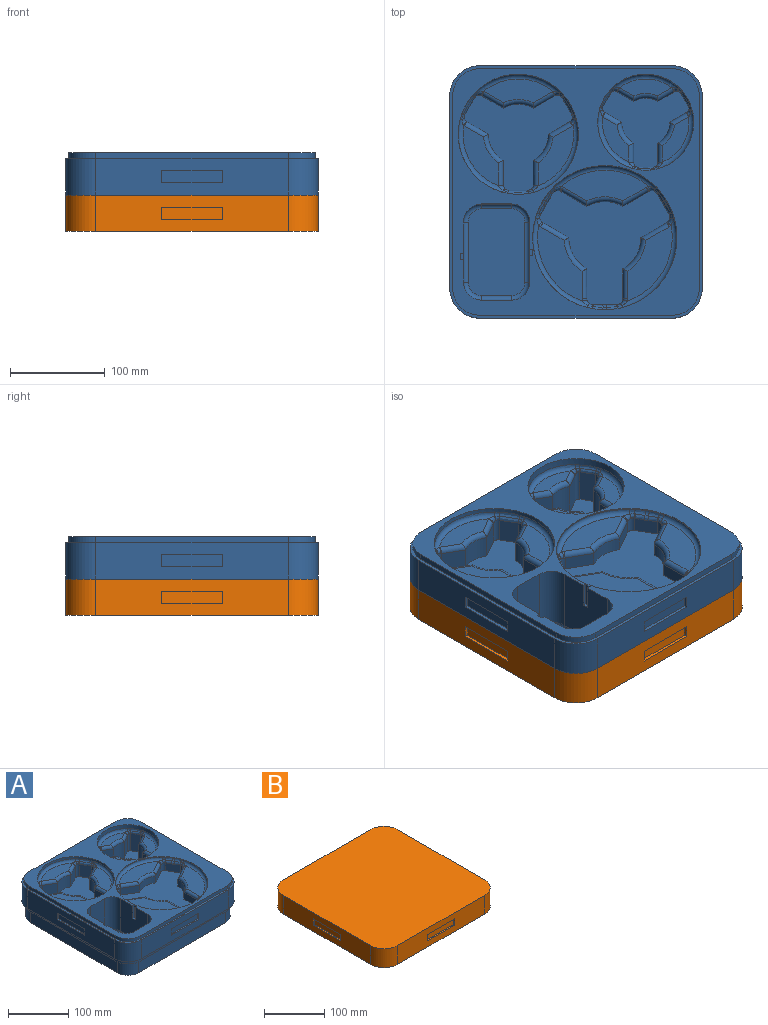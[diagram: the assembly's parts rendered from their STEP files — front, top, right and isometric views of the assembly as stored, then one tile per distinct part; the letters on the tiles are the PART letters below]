
ASSEMBLY  parts=2 mates=1
PART A: 313 faces, bbox 266.7x266.7x78.5 mm
  f0: plane 260.35x260.35mm, normal (0,0,1), area 21239.2mm2, adj f1,f17,f38,f59,f79,f80,f81,f82
  f1: plane 66.04x63.5mm, normal (-1,0,0), area 4032.2mm2, adj f0,f80,f81,f87,f309,f310,f312
  f2: plane 203.2x38.1mm, normal (1,0,0), area 6935.5mm2, adj f6,f9,f265,f274,f300,f301,f302,f303
  f3: plane 203.2x38.1mm, normal (0,1,0), area 6935.5mm2, adj f8,f9,f265,f274,f295,f296,f297,f298
  f4: plane 203.2x38.1mm, normal (-1,0,0), area 6935.5mm2, adj f7,f8,f265,f274,f290,f291,f292,f293
  f5: plane 203.2x38.1mm, normal (0,-1,0), area 6935.5mm2, adj f6,f7,f265,f274,f285,f286,f287,f288
  f6: cylinder r=31.75mm len=38.1mm, axis (0,0,1), area 1900.2mm2, adj f2,f5,f265,f274
  f7: cylinder r=31.75mm len=38.1mm, axis (0,0,1), area 1900.2mm2, adj f4,f5,f265,f274
  f8: cylinder r=31.75mm len=38.1mm, axis (0,0,1), area 1900.2mm2, adj f3,f4,f265,f274
  f9: cylinder r=31.75mm len=38.1mm, axis (0,0,1), area 1900.2mm2, adj f2,f3,f265,f274
  f10: plane 55.18x17.94mm, normal (0,0,1), area 651.1mm2, adj f131,f224,f226,f228
  f11: plane 47.78x27.94mm, normal (0,0,1), area 651.1mm2, adj f126,f229,f231,f233
  f12: plane 73.54x25.13mm, normal (0,0,1), area 1214.4mm2, adj f119,f184,f186,f188,f190,f192
  f13: plane 63.69x37.49mm, normal (0,0,1), area 1214.4mm2, adj f114,f189,f191,f193,f195,f197
  f14: plane 92.17x32.32mm, normal (0,0,1), area 1949.1mm2, adj f103,f173,f175,f176,f177,f178
  f15: plane 79.82x47.25mm, normal (0,0,1), area 1949.1mm2, adj f98,f145,f147,f149,f151,f153
  f16: plane 47.78x27.94mm, normal (0,0,1), area 651.1mm2, adj f134,f252,f254,f256
  f17: cylinder r=50.8mm len=101.6mm, axis (0,0,1), area 2476.3mm2, adj f0,f125,f126,f127,f128,f129,f130,f131
  f18: plane 91.6x80.5mm, normal (0,0,1), area 3762.4mm2, adj f19,f20,f21,f22,f23,f24,f25,f26
  f19: plane 33.06x18.21mm, normal (0.5,0.87,0), area 694.5mm2, adj f18,f20,f36,f227,f229
  f20: cylinder r=4.37mm len=35.74mm, axis (0,0,1), area 238.6mm2, adj f18,f19,f21,f219,f221,f223,f225
  f21: plane 35.69x14.43mm, normal (0.87,-0.5,0), area 590.4mm2, adj f18,f20,f22,f217
  f22: cylinder r=4.37mm len=35.74mm, axis (0,0,1), area 238.6mm2, adj f18,f21,f23,f215,f216,f218,f220
  f23: plane 33.06x18.21mm, normal (-0.5,-0.87,0), area 694.5mm2, adj f18,f22,f24,f222,f224
  f24: cylinder r=25.4mm len=33.02mm, axis (0,0,1), area 878.3mm2, adj f18,f23,f25,f226
  f25: plane 33.06x18.21mm, normal (0.5,-0.87,0), area 694.5mm2, adj f18,f24,f26,f228,f230
  f26: cylinder r=4.37mm len=35.74mm, axis (0,0,1), area 238.6mm2, adj f18,f25,f27,f232,f234,f236,f238
  f27: plane 35.7x14.44mm, normal (-0.87,-0.5,0), area 590.4mm2, adj f18,f26,f28,f240
  f28: cylinder r=4.37mm len=35.74mm, axis (0,0,1), area 238.6mm2, adj f18,f27,f29,f242,f244,f246,f248
  f29: plane 33.06x18.21mm, normal (-0.5,0.87,0), area 694.5mm2, adj f18,f28,f30,f250,f252
  f30: cylinder r=25.4mm len=33.02mm, axis (0,0,1), area 878.3mm2, adj f18,f29,f31,f254
  f31: plane 33.06x21.03mm, normal (-1,0,0), area 694.5mm2, adj f18,f30,f32,f255,f256
  f32: cylinder r=4.37mm len=35.74mm, axis (0,0,1), area 238.6mm2, adj f18,f31,f33,f247,f249,f251,f253
  f33: plane 35.69x16.66mm, normal (0,1,0), area 590.4mm2, adj f18,f32,f34,f245
  f34: cylinder r=4.37mm len=35.74mm, axis (0,0,1), area 238.6mm2, adj f18,f33,f35,f237,f239,f241,f243
  f35: plane 33.06x21.03mm, normal (1,0,0), area 694.5mm2, adj f18,f34,f36,f233,f235
  f36: cylinder r=25.4mm len=33.02mm, axis (0,0,1), area 878.3mm2, adj f18,f19,f35,f231
  f37: plane 63.69x37.49mm, normal (0,0,1), area 1214.4mm2, adj f122,f208,f210,f212,f213,f214
  f38: cylinder r=63.5mm len=127mm, axis (0,0,1), area 1800.1mm2, adj f0,f113,f114,f115,f116,f117,f118,f119
  f39: plane 114.5x100.62mm, normal (0,0,1), area 5878.8mm2, adj f40,f41,f42,f43,f44,f45,f46,f47
  f40: plane 23.5x22.77mm, normal (0.5,0.87,0), area 617.7mm2, adj f39,f41,f57,f191
  f41: cylinder r=5.46mm len=25.84mm, axis (0,0,1), area 212.8mm2, adj f39,f40,f42,f183,f185,f187,f189
  f42: plane 25.8x18.04mm, normal (0.87,-0.5,0), area 530.7mm2, adj f39,f41,f43,f181
  f43: cylinder r=5.46mm len=25.84mm, axis (0,0,1), area 212.8mm2, adj f39,f42,f44,f179,f180,f182,f184
  f44: plane 23.5x22.77mm, normal (-0.5,-0.87,0), area 617.7mm2, adj f39,f43,f45,f186
  f45: cylinder r=31.75mm len=31.75mm, axis (0,0,1), area 781.2mm2, adj f39,f44,f46,f188
  f46: plane 23.5x22.77mm, normal (0.5,-0.87,0), area 617.7mm2, adj f39,f45,f47,f190
  f47: cylinder r=5.46mm len=25.84mm, axis (0,0,1), area 212.8mm2, adj f39,f46,f48,f192,f194,f196,f198
  f48: plane 25.8x18.05mm, normal (-0.87,-0.5,0), area 530.7mm2, adj f39,f47,f49,f200
  f49: cylinder r=5.46mm len=25.84mm, axis (0,0,1), area 212.8mm2, adj f39,f48,f50,f202,f204,f206,f208
  f50: plane 23.5x22.77mm, normal (-0.5,0.87,0), area 617.7mm2, adj f39,f49,f51,f210
  f51: cylinder r=31.75mm len=27.5mm, axis (0,0,1), area 781.2mm2, adj f39,f50,f52,f212
  f52: plane 26.29x23.5mm, normal (-1,0,0), area 617.7mm2, adj f39,f51,f53,f214
  f53: cylinder r=5.46mm len=25.84mm, axis (0,0,1), area 212.8mm2, adj f39,f52,f54,f207,f209,f211,f213
  f54: plane 25.8x20.83mm, normal (0,1,0), area 530.7mm2, adj f39,f53,f55,f205
  f55: cylinder r=5.46mm len=25.84mm, axis (0,0,1), area 212.8mm2, adj f39,f54,f56,f197,f199,f201,f203
  f56: plane 26.29x23.5mm, normal (1,0,0), area 617.7mm2, adj f39,f55,f57,f195
  f57: cylinder r=31.75mm len=27.5mm, axis (0,0,1), area 781.2mm2, adj f39,f40,f56,f193
  f58: plane 79.82x47.25mm, normal (0,0,1), area 1949.1mm2, adj f110,f148,f150,f152,f154,f156
  f59: cylinder r=76.2mm len=152.4mm, axis (0,0,1), area 613.9mm2, adj f0,f95,f96,f97,f98,f99,f100,f101
  f60: plane 137.39x120.74mm, normal (0,0,1), area 8465.4mm2, adj f61,f62,f63,f64,f65,f66,f67,f68
  f61: plane 31.55x13.97mm, normal (1,0,0), area 440.7mm2, adj f60,f62,f78,f147
  f62: cylinder r=38.1mm len=33mm, axis (0,0,1), area 557.4mm2, adj f60,f61,f63,f149
  f63: plane 27.32x15.77mm, normal (0.5,0.87,0), area 440.7mm2, adj f60,f62,f64,f151
  f64: cylinder r=6.55mm len=15.95mm, axis (0,0,1), area 154.1mm2, adj f60,f63,f65,f153,f155,f157,f159
  f65: plane 21.65x15.9mm, normal (0.87,-0.5,0), area 387.7mm2, adj f60,f64,f66,f161,f163,f165
  f66: cylinder r=6.55mm len=15.95mm, axis (0,0,1), area 154.1mm2, adj f60,f65,f67,f167,f169,f171,f173
  f67: plane 27.32x15.77mm, normal (-0.5,-0.87,0), area 440.7mm2, adj f60,f66,f68,f175
  f68: cylinder r=38.1mm len=38.1mm, axis (0,0,1), area 557.4mm2, adj f60,f67,f69,f177
  f69: plane 27.32x15.77mm, normal (0.5,-0.87,0), area 440.7mm2, adj f60,f68,f70,f178
  f70: cylinder r=6.55mm len=15.95mm, axis (0,0,1), area 154.1mm2, adj f60,f69,f71,f170,f172,f174,f176
  f71: plane 21.65x15.9mm, normal (-0.87,-0.5,0), area 387.7mm2, adj f60,f70,f72,f164,f166,f168
  f72: cylinder r=6.55mm len=15.95mm, axis (0,0,1), area 154.1mm2, adj f60,f71,f73,f156,f158,f160,f162
  f73: plane 27.32x15.77mm, normal (-0.5,0.87,0), area 440.7mm2, adj f60,f72,f74,f154
  f74: cylinder r=38.1mm len=33mm, axis (0,0,1), area 557.4mm2, adj f60,f73,f75,f152
  f75: plane 31.55x13.97mm, normal (-1,0,0), area 440.7mm2, adj f60,f74,f76,f150
  f76: cylinder r=6.55mm len=15.95mm, axis (0,0,1), area 154.1mm2, adj f60,f75,f77,f142,f144,f146,f148
  f77: plane 25x15.9mm, normal (0,1,0), area 387.7mm2, adj f60,f76,f78,f137,f138,f140
  f78: cylinder r=6.55mm len=15.95mm, axis (0,0,1), area 154.1mm2, adj f60,f61,f77,f139,f141,f143,f145
  f79: plane 66.04x31.75mm, normal (0,1,0), area 2096.8mm2, adj f0,f80,f85,f91
  f80: cylinder r=19.05mm len=66.04mm, axis (0,0,1), area 1976.2mm2, adj f0,f1,f79,f89
  f81: cylinder r=19.05mm len=66.04mm, axis (0,0,1), area 1976.2mm2, adj f0,f1,f82,f88
  f82: plane 66.04x31.75mm, normal (0,-1,0), area 2096.8mm2, adj f0,f81,f83,f90
  f83: cylinder r=19.05mm len=66.04mm, axis (0,0,1), area 1976.2mm2, adj f0,f82,f84,f92
  f84: plane 66.04x63.5mm, normal (1,0,0), area 4032.3mm2, adj f0,f83,f85,f94,f305,f307,f308
  f85: cylinder r=19.05mm len=66.04mm, axis (0,0,1), area 1976.2mm2, adj f0,f79,f84,f93
  f86: plane 91.44x59.69mm, normal (0,0,1), area 5290.5mm2, adj f87,f88,f89,f90,f91,f92,f93,f94
  f87: cylinder r=5.08mm len=63.5mm, axis (0,1,0), area 506.7mm2, adj f1,f86,f88,f89
  f88: torus R=13.97mm, axis (0,0,1), area 215.6mm2, adj f81,f86,f87,f90
  f89: torus R=13.97mm, axis (0,0,1), area 215.6mm2, adj f80,f86,f87,f91
  f90: cylinder r=5.08mm len=31.75mm, axis (-1,0,0), area 253.4mm2, adj f82,f86,f88,f92
  f91: cylinder r=5.08mm len=31.75mm, axis (1,0,0), area 253.4mm2, adj f79,f86,f89,f93
  f92: torus R=13.97mm, axis (0,0,1), area 215.6mm2, adj f83,f86,f90,f94
  f93: torus R=13.97mm, axis (0,0,1), area 215.6mm2, adj f85,f86,f91,f94
  f94: cylinder r=5.08mm len=63.5mm, axis (0,-1,0), area 506.7mm2, adj f84,f86,f92,f93
  f95: bspline ~17.19x11.79mm, area 57.1mm2, adj f59,f96,f97,f159,f161
  f96: bspline ~7.71x6.01mm, area 24.7mm2, adj f59,f95,f98,f157
  f97: torus R=71.12mm, axis (0,0,1), area 21mm2, adj f59,f95,f99,f163
  f98: torus R=71.12mm, axis (0,0,1), area 930.2mm2, adj f15,f59,f96,f100,f143,f155
  f99: bspline ~14.9x11.49mm, area 57.1mm2, adj f59,f97,f101,f165,f167
  f100: bspline ~7.36x6.51mm, area 24.7mm2, adj f59,f98,f102,f141
  f101: bspline ~8.2x7.73mm, area 24.7mm2, adj f59,f99,f103,f169
  f102: bspline ~15.1x5.11mm, area 57.1mm2, adj f59,f100,f104,f137,f139
  f103: torus R=71.12mm, axis (0,0,1), area 930.2mm2, adj f14,f59,f101,f105,f171,f174
  f104: torus R=71.12mm, axis (0,0,1), area 21mm2, adj f59,f102,f106,f138
  f105: bspline ~8.27x7.77mm, area 24.7mm2, adj f59,f103,f107,f172
  f106: bspline ~18.01x5.11mm, area 57.1mm2, adj f59,f104,f108,f140,f142
  f107: bspline ~17.15x12.87mm, area 57.1mm2, adj f59,f105,f109,f168,f170
  f108: bspline ~7.45x6.62mm, area 24.7mm2, adj f59,f106,f110,f144
  f109: torus R=71.12mm, axis (0,0,1), area 21mm2, adj f59,f107,f111,f166
  f110: torus R=71.12mm, axis (0,0,1), area 930.2mm2, adj f58,f59,f108,f112,f146,f158
  f111: bspline ~14.79x10.74mm, area 57.1mm2, adj f59,f109,f112,f162,f164
  f112: bspline ~7.69x6.02mm, area 24.7mm2, adj f59,f110,f111,f160
  f113: bspline ~7.36x5.26mm, area 23.2mm2, adj f38,f114,f115,f185
  f114: torus R=58.42mm, axis (0,0,1), area 751.7mm2, adj f13,f38,f113,f116,f187,f199
  f115: bspline ~23.49x15.24mm, area 103.3mm2, adj f38,f113,f117,f179,f181,f183
  f116: bspline ~7.62x6.6mm, area 23.2mm2, adj f38,f114,f118,f201
  f117: bspline ~8.28x7.58mm, area 23.2mm2, adj f38,f115,f119,f180
  f118: bspline ~26.54x5.01mm, area 103.3mm2, adj f38,f116,f120,f203,f205,f207
  f119: torus R=58.42mm, axis (0,0,1), area 751.7mm2, adj f12,f38,f117,f121,f182,f194
  f120: bspline ~7.09x6.44mm, area 23.2mm2, adj f38,f118,f122,f209
  f121: bspline ~7.97x7.13mm, area 23.2mm2, adj f38,f119,f123,f196
  f122: torus R=58.42mm, axis (0,0,1), area 751.7mm2, adj f37,f38,f120,f124,f206,f211
  f123: bspline ~23.5x15.19mm, area 103.3mm2, adj f38,f121,f124,f198,f200,f202
  f124: bspline ~7.75x5.51mm, area 23.2mm2, adj f38,f122,f123,f204
  f125: bspline ~6.65x5.33mm, area 20.4mm2, adj f17,f126,f127,f221,f223
  f126: torus R=45.72mm, axis (0,0,1), area 575.4mm2, adj f11,f17,f125,f128,f225,f227,f235,f237
  f127: bspline ~18.49x12.09mm, area 74.2mm2, adj f17,f125,f129,f215,f217,f219
  f128: bspline ~6.77x6.31mm, area 20.4mm2, adj f17,f126,f130,f239,f241
  f129: bspline ~7.62x6.56mm, area 20.4mm2, adj f17,f127,f131,f216,f218
  f130: bspline ~21.1x4.8mm, area 74.2mm2, adj f17,f128,f132,f243,f245,f247
  f131: torus R=45.72mm, axis (0,0,1), area 575.4mm2, adj f10,f17,f129,f133,f220,f222,f230,f232
  f132: bspline ~6.73x6.38mm, area 20.4mm2, adj f17,f130,f134,f249,f251
  f133: bspline ~7.53x6.45mm, area 20.4mm2, adj f17,f131,f135,f234,f236
  f134: torus R=45.72mm, axis (0,0,1), area 575.4mm2, adj f16,f17,f132,f136,f248,f250,f253,f255
  f135: bspline ~18.52x11.93mm, area 74.2mm2, adj f17,f133,f136,f238,f240,f242
  f136: bspline ~6.88x5.21mm, area 20.4mm2, adj f17,f134,f135,f244,f246
  f137: bspline ~14.38x4.67mm, area 52.8mm2, adj f77,f102,f138,f139
  f138: bspline ~9x4.47mm, area 20.9mm2, adj f77,f104,f137,f140
  f139: bspline ~4.3x3.11mm, area 2.8mm2, adj f78,f102,f137,f141
  f140: bspline ~16.91x4.74mm, area 52.8mm2, adj f77,f106,f138,f142
  f141: bspline ~5.18x4.35mm, area 19.7mm2, adj f78,f100,f139,f143
  f142: bspline ~4.51x4.47mm, area 2.8mm2, adj f76,f106,f140,f144
  f143: bspline ~9.19x6.77mm, area 38.2mm2, adj f78,f98,f141,f145
  f144: bspline ~5.97x4.39mm, area 19.8mm2, adj f76,f108,f142,f146
  f145: torus R=11.63mm, axis (0,0,1), area 14.2mm2, adj f15,f78,f143,f147
  f146: bspline ~9.56x7.54mm, area 38.2mm2, adj f76,f110,f144,f148
  f147: cylinder r=5.08mm len=31.55mm, axis (0,-1,0), area 240.5mm2, adj f15,f61,f145,f149
  f148: torus R=11.63mm, axis (0,0,1), area 14.2mm2, adj f58,f76,f146,f150
  f149: torus R=43.18mm, axis (0,0,1), area 311.2mm2, adj f15,f62,f147,f151
  f150: cylinder r=5.08mm len=31.55mm, axis (0,1,0), area 240.5mm2, adj f58,f75,f148,f152
  f151: cylinder r=5.08mm len=29.86mm, axis (0.87,-0.5,0), area 240.5mm2, adj f15,f63,f149,f153
  f152: torus R=43.18mm, axis (0,0,1), area 311.2mm2, adj f58,f74,f150,f154
  f153: torus R=11.63mm, axis (0,0,1), area 14.2mm2, adj f15,f64,f151,f155
  f154: cylinder r=5.08mm len=29.86mm, axis (0.87,0.5,0), area 240.5mm2, adj f58,f73,f152,f156
  f155: bspline ~10.65x6.1mm, area 38.2mm2, adj f64,f98,f153,f157
  f156: torus R=11.63mm, axis (0,0,1), area 14.2mm2, adj f58,f72,f154,f158
  f157: bspline ~5.95x4.39mm, area 19.8mm2, adj f64,f96,f155,f159
  f158: bspline ~10.65x6.1mm, area 38.2mm2, adj f72,f110,f156,f160
  f159: bspline ~4.66x4.47mm, area 2.8mm2, adj f64,f95,f157,f161
  f160: bspline ~5.96x4.39mm, area 19.8mm2, adj f72,f112,f158,f162
  f161: bspline ~15.88x9.79mm, area 52.8mm2, adj f65,f95,f159,f163
  f162: bspline ~4.3x3.27mm, area 2.8mm2, adj f72,f111,f160,f164
  f163: bspline ~11.44x8.02mm, area 20.9mm2, adj f65,f97,f161,f165
  f164: bspline ~13.69x8.75mm, area 52.8mm2, adj f71,f111,f162,f166
  f165: bspline ~13.13x9.38mm, area 52.8mm2, adj f65,f99,f163,f167
  f166: bspline ~11.44x8.02mm, area 20.9mm2, adj f71,f109,f164,f168
  f167: bspline ~4.3x3.32mm, area 2.8mm2, adj f66,f99,f165,f169
  f168: bspline ~15.16x10.64mm, area 52.8mm2, adj f71,f107,f166,f170
  f169: bspline ~4.78x4.64mm, area 19.7mm2, adj f66,f101,f167,f171
  f170: bspline ~4.47x4.22mm, area 2.8mm2, adj f70,f107,f168,f172
  f171: bspline ~8.96x6.1mm, area 38.2mm2, adj f66,f103,f169,f173
  f172: bspline ~5.34x5.17mm, area 19.8mm2, adj f70,f105,f170,f174
  f173: torus R=11.63mm, axis (0,0,1), area 14.2mm2, adj f14,f66,f171,f175
  f174: bspline ~9.83x6.1mm, area 38.2mm2, adj f70,f103,f172,f176
  f175: cylinder r=5.08mm len=29.86mm, axis (-0.87,0.5,0), area 240.5mm2, adj f14,f67,f173,f177
  f176: torus R=11.63mm, axis (0,0,1), area 14.2mm2, adj f14,f70,f174,f178
  f177: torus R=43.18mm, axis (0,0,1), area 311.2mm2, adj f14,f68,f175,f178
  f178: cylinder r=5.08mm len=29.86mm, axis (-0.87,-0.5,0), area 240.5mm2, adj f14,f69,f176,f177
  f179: bspline ~4x2.81mm, area 2.3mm2, adj f43,f115,f180,f181
  f180: bspline ~4.8x4.71mm, area 18.3mm2, adj f43,f117,f179,f182
  f181: bspline ~20.94x13.01mm, area 95.3mm2, adj f42,f115,f179,f183
  f182: bspline ~9.08x6.3mm, area 34.2mm2, adj f43,f119,f180,f184
  f183: bspline ~4.17x3.97mm, area 2.3mm2, adj f41,f115,f181,f185
  f184: torus R=10.54mm, axis (0,0,1), area 4.2mm2, adj f12,f43,f182,f186
  f185: bspline ~5.81x4.17mm, area 18.3mm2, adj f41,f113,f183,f187
  f186: cylinder r=5.08mm len=25.31mm, axis (-0.87,0.5,0), area 198.6mm2, adj f12,f44,f184,f188
  f187: bspline ~9.84x6.3mm, area 34.2mm2, adj f41,f114,f185,f189
  f188: torus R=36.83mm, axis (0,0,1), area 258.3mm2, adj f12,f45,f186,f190
  f189: torus R=10.54mm, axis (0,0,1), area 4.2mm2, adj f13,f41,f187,f191
  f190: cylinder r=5.08mm len=25.31mm, axis (-0.87,-0.5,0), area 198.6mm2, adj f12,f46,f188,f192
  f191: cylinder r=5.08mm len=25.31mm, axis (0.87,-0.5,0), area 198.6mm2, adj f13,f40,f189,f193
  f192: torus R=10.54mm, axis (0,0,1), area 4.2mm2, adj f12,f47,f190,f194
  f193: torus R=36.83mm, axis (0,0,1), area 258.3mm2, adj f13,f57,f191,f195
  f194: bspline ~9.08x6.3mm, area 34.2mm2, adj f47,f119,f192,f196
  f195: cylinder r=5.08mm len=26.29mm, axis (0,-1,0), area 198.6mm2, adj f13,f56,f193,f197
  f196: bspline ~4.94x4.84mm, area 18.3mm2, adj f47,f121,f194,f198
  f197: torus R=10.54mm, axis (0,0,1), area 4.2mm2, adj f13,f55,f195,f199
  f198: bspline ~4.17x3.53mm, area 2.3mm2, adj f47,f123,f196,f200
  f199: bspline ~8.21x6.3mm, area 34.2mm2, adj f55,f114,f197,f201
  f200: bspline ~21.8x13.42mm, area 95.3mm2, adj f48,f123,f198,f202
  f201: bspline ~5.65x4.16mm, area 18.3mm2, adj f55,f116,f199,f203
  f202: bspline ~4x3.03mm, area 2.3mm2, adj f49,f123,f200,f204
  f203: bspline ~4x2.24mm, area 2.3mm2, adj f55,f118,f201,f205
  f204: bspline ~5.73x4.16mm, area 18.3mm2, adj f49,f124,f202,f206
  f205: bspline ~23.64x4.29mm, area 95.3mm2, adj f54,f118,f203,f207
  f206: bspline ~9.31x6.3mm, area 34.2mm2, adj f49,f122,f204,f208
  f207: bspline ~4.17x3.85mm, area 2.3mm2, adj f53,f118,f205,f209
  f208: torus R=10.54mm, axis (0,0,1), area 4.2mm2, adj f37,f49,f206,f210
  f209: bspline ~5.73x4.17mm, area 18.3mm2, adj f53,f120,f207,f211
  f210: cylinder r=5.08mm len=25.31mm, axis (0.87,0.5,0), area 198.6mm2, adj f37,f50,f208,f212
  f211: bspline ~8.4x6.77mm, area 34.2mm2, adj f53,f122,f209,f213
  f212: torus R=36.83mm, axis (0,0,1), area 258.3mm2, adj f37,f51,f210,f214
  f213: torus R=10.54mm, axis (0,0,1), area 4.2mm2, adj f37,f53,f211,f214
  f214: cylinder r=5.08mm len=26.29mm, axis (0,1,0), area 198.6mm2, adj f37,f52,f212,f213
  f215: bspline ~3.6x2.36mm, area 1.9mm2, adj f22,f127,f216,f217
  f216: bspline ~4.17x4.11mm, area 13.7mm2, adj f22,f129,f215,f218
  f217: bspline ~18.95x11.73mm, area 67.5mm2, adj f21,f127,f215,f219
  f218: bspline ~3.89x2.42mm, area 1.2mm2, adj f22,f129,f216,f220
  f219: bspline ~3.6x2.65mm, area 1.9mm2, adj f20,f127,f217,f221
  f220: bspline ~7.81x6.47mm, area 28.9mm2, adj f22,f131,f218,f222
  f221: bspline ~5.04x3.84mm, area 13.5mm2, adj f20,f125,f219,f223
  f222: bspline ~5.99x5.69mm, area 5.2mm2, adj f23,f131,f220,f224
  f223: bspline ~3.89x1.84mm, area 1.4mm2, adj f20,f125,f221,f225
  f224: cylinder r=5.08mm len=19.97mm, axis (-0.87,0.5,0), area 149.6mm2, adj f10,f23,f222,f226
  f225: bspline ~8.2x6.46mm, area 28.9mm2, adj f20,f126,f223,f227
  f226: torus R=30.48mm, axis (0,0,1), area 205.4mm2, adj f10,f24,f224,f228
  f227: bspline ~5.91x5.49mm, area 5.2mm2, adj f19,f126,f225,f229
  f228: cylinder r=5.08mm len=19.97mm, axis (-0.87,-0.5,0), area 149.6mm2, adj f10,f25,f226,f230
  f229: cylinder r=5.08mm len=19.97mm, axis (0.87,-0.5,0), area 149.6mm2, adj f11,f19,f227,f231
  f230: bspline ~5.99x5.69mm, area 5.2mm2, adj f25,f131,f228,f232
  f231: torus R=30.48mm, axis (0,0,1), area 205.4mm2, adj f11,f36,f229,f233
  f232: bspline ~7.81x6.47mm, area 28.9mm2, adj f26,f131,f230,f234
  f233: cylinder r=5.08mm len=20.12mm, axis (0,-1,0), area 149.6mm2, adj f11,f35,f231,f235
  f234: bspline ~3.89x2.43mm, area 1.4mm2, adj f26,f133,f232,f236
  f235: bspline ~5.49x5.43mm, area 5.2mm2, adj f35,f126,f233,f237
  f236: bspline ~4.14x4.09mm, area 13.5mm2, adj f26,f133,f234,f238
  f237: bspline ~6.97x6.46mm, area 28.9mm2, adj f34,f126,f235,f239
  f238: bspline ~3.82x3.04mm, area 1.9mm2, adj f26,f135,f236,f240
  f239: bspline ~3.89x2.39mm, area 1.2mm2, adj f34,f128,f237,f241
  f240: bspline ~17.63x10.89mm, area 67.5mm2, adj f27,f135,f238,f242
  f241: bspline ~4.71x3.85mm, area 13.7mm2, adj f34,f128,f239,f243
  f242: bspline ~3.82x3.38mm, area 1.9mm2, adj f28,f135,f240,f244
  f243: bspline ~3.6x2.44mm, area 1.9mm2, adj f34,f130,f241,f245
  f244: bspline ~4.84x3.85mm, area 13.7mm2, adj f28,f136,f242,f246
  f245: bspline ~21.71x3.85mm, area 67.5mm2, adj f33,f130,f243,f247
  f246: bspline ~3.89x1.84mm, area 1.2mm2, adj f28,f136,f244,f248
  f247: bspline ~3.6x2.53mm, area 1.9mm2, adj f32,f130,f245,f249
  f248: bspline ~8.2x6.46mm, area 28.9mm2, adj f28,f134,f246,f250
  f249: bspline ~4.96x3.83mm, area 13.5mm2, adj f32,f132,f247,f251
  f250: bspline ~5.91x5.49mm, area 5.2mm2, adj f29,f134,f248,f252
  f251: bspline ~3.89x2.4mm, area 1.4mm2, adj f32,f132,f249,f253
  f252: cylinder r=5.08mm len=19.97mm, axis (0.87,0.5,0), area 149.6mm2, adj f16,f29,f250,f254
  f253: bspline ~6.97x6.46mm, area 28.9mm2, adj f32,f134,f251,f255
  f254: torus R=30.48mm, axis (0,0,1), area 205.4mm2, adj f16,f30,f252,f256
  f255: bspline ~5.49x5.43mm, area 5.2mm2, adj f31,f134,f253,f256
  f256: cylinder r=5.08mm len=20.12mm, axis (0,1,0), area 149.6mm2, adj f16,f31,f254,f255
  f257: cylinder r=28.57mm len=28.58mm, axis (0,0,1), area 285mm2, adj f0,f258,f264,f265
  f258: plane 203.2x6.35mm, normal (-1,0,0), area 1290.3mm2, adj f0,f257,f259,f265
  f259: cylinder r=28.57mm len=28.58mm, axis (0,0,1), area 285mm2, adj f0,f258,f260,f265
  f260: plane 203.2x6.35mm, normal (0,1,0), area 1290.3mm2, adj f0,f259,f261,f265
  f261: cylinder r=28.57mm len=28.58mm, axis (0,0,1), area 285mm2, adj f0,f260,f262,f265
  f262: plane 203.2x6.35mm, normal (1,0,0), area 1290.3mm2, adj f0,f261,f263,f265
  f263: cylinder r=28.57mm len=28.58mm, axis (0,0,1), area 285mm2, adj f0,f262,f264,f265
  f264: plane 203.2x6.35mm, normal (0,-1,0), area 1290.3mm2, adj f0,f257,f263,f265
  f265: plane 266.7x266.7mm, normal (0,0,1), area 3182.4mm2, adj f2,f3,f4,f5,f6,f7,f8,f9
  f266: plane 203.2x6.35mm, normal (0,-1,0), area 1290.3mm2, adj f267,f273,f274,f284
  f267: cylinder r=28.57mm len=28.58mm, axis (0,0,-1), area 285mm2, adj f266,f268,f274,f284
  f268: plane 203.2x6.35mm, normal (1,0,0), area 1290.3mm2, adj f267,f269,f274,f284
  f269: cylinder r=28.57mm len=28.58mm, axis (0,0,-1), area 285mm2, adj f268,f270,f274,f284
  f270: plane 203.2x6.35mm, normal (0,1,0), area 1290.3mm2, adj f269,f271,f274,f284
  f271: cylinder r=28.57mm len=28.58mm, axis (0,0,-1), area 285mm2, adj f270,f272,f274,f284
  f272: plane 203.2x6.35mm, normal (-1,0,0), area 1290.3mm2, adj f271,f273,f274,f284
  f273: cylinder r=28.57mm len=28.58mm, axis (0,0,-1), area 285mm2, adj f266,f272,f274,f284
  f274: plane 266.7x266.7mm, normal (0,0,-1), area 3182.4mm2, adj f2,f3,f4,f5,f6,f7,f8,f9
  f275: plane 254x254mm, normal (0,0,-1), area 63962.2mm2, adj f276,f277,f278,f279,f280,f281,f282,f283
  f276: plane 203.2x25.4mm, normal (-1,0,0), area 5161.3mm2, adj f275,f277,f283,f284
  f277: cylinder r=25.4mm len=25.4mm, axis (0,0,-1), area 1013.4mm2, adj f275,f276,f278,f284
  f278: plane 203.2x25.4mm, normal (0,1,0), area 5161.3mm2, adj f275,f277,f279,f284
  f279: cylinder r=25.4mm len=25.4mm, axis (0,0,-1), area 1013.4mm2, adj f275,f278,f280,f284
  f280: plane 203.2x25.4mm, normal (1,0,0), area 5161.3mm2, adj f275,f279,f281,f284
  f281: cylinder r=25.4mm len=25.4mm, axis (0,0,-1), area 1013.4mm2, adj f275,f280,f282,f284
  f282: plane 203.2x25.4mm, normal (0,-1,0), area 5161.3mm2, adj f275,f281,f283,f284
  f283: cylinder r=25.4mm len=25.4mm, axis (0,0,-1), area 1013.4mm2, adj f275,f276,f282,f284
  f284: plane 260.35x260.35mm, normal (0,0,-1), area 3119mm2, adj f266,f267,f268,f269,f270,f271,f272,f273
  f285: plane 63.5x3.18mm, normal (0,0,1), area 201.6mm2, adj f5,f286,f288,f289
  f286: plane 12.7x3.18mm, normal (-1,0,0), area 40.3mm2, adj f5,f285,f287,f289
  f287: plane 63.5x3.18mm, normal (0,0,-1), area 201.6mm2, adj f5,f286,f288,f289
  f288: plane 12.7x3.18mm, normal (1,0,0), area 40.3mm2, adj f5,f285,f287,f289
  f289: plane 63.5x12.7mm, normal (0,-1,0), area 806.4mm2, adj f285,f286,f287,f288
  f290: plane 12.7x3.18mm, normal (0,1,0), area 40.3mm2, adj f4,f291,f293,f294
  f291: plane 63.5x3.18mm, normal (0,0,-1), area 201.6mm2, adj f4,f290,f292,f294
  f292: plane 12.7x3.18mm, normal (0,-1,0), area 40.3mm2, adj f4,f291,f293,f294
  f293: plane 63.5x3.18mm, normal (0,0,1), area 201.6mm2, adj f4,f290,f292,f294
  f294: plane 63.5x12.7mm, normal (-1,0,0), area 806.4mm2, adj f290,f291,f292,f293
  f295: plane 12.7x3.18mm, normal (1,0,0), area 40.3mm2, adj f3,f296,f298,f299
  f296: plane 63.5x3.18mm, normal (0,0,-1), area 201.6mm2, adj f3,f295,f297,f299
  f297: plane 12.7x3.18mm, normal (-1,0,0), area 40.3mm2, adj f3,f296,f298,f299
  f298: plane 63.5x3.18mm, normal (0,0,1), area 201.6mm2, adj f3,f295,f297,f299
  f299: plane 63.5x12.7mm, normal (0,1,0), area 806.5mm2, adj f295,f296,f297,f298
  f300: plane 12.7x3.18mm, normal (0,-1,0), area 40.3mm2, adj f2,f301,f303,f304
  f301: plane 63.5x3.18mm, normal (0,0,-1), area 201.6mm2, adj f2,f300,f302,f304
  f302: plane 12.7x3.18mm, normal (0,1,0), area 40.3mm2, adj f2,f301,f303,f304
  f303: plane 63.5x3.18mm, normal (0,0,1), area 201.6mm2, adj f2,f300,f302,f304
  f304: plane 63.5x12.7mm, normal (1,0,0), area 806.4mm2, adj f300,f301,f302,f303
  f305: plane 25.4x3.18mm, normal (0,-1,0), area 80.6mm2, adj f0,f84,f306,f308
  f306: plane 25.4x6.35mm, normal (1,0,0), area 161.3mm2, adj f0,f305,f307,f308
  f307: plane 25.4x3.18mm, normal (0,1,0), area 80.6mm2, adj f0,f84,f306,f308
  f308: plane 6.35x3.18mm, normal (0,0,1), area 20.2mm2, adj f84,f305,f306,f307
  f309: plane 25.4x3.18mm, normal (0,-1,0), area 80.6mm2, adj f0,f1,f311,f312
  f310: plane 25.4x3.18mm, normal (0,1,0), area 80.6mm2, adj f0,f1,f311,f312
  f311: plane 25.4x6.35mm, normal (-1,0,0), area 161.3mm2, adj f0,f309,f310,f312
  f312: plane 6.35x3.18mm, normal (0,0,1), area 20.2mm2, adj f1,f309,f310,f311
PART B: 48 faces, bbox 266.7x266.7x38.1 mm
  f0: plane 203.2x38.1mm, normal (1,0,0), area 6935.5mm2, adj f22,f23,f25,f26,f43,f44,f45,f46
  f1: plane 203.2x38.1mm, normal (0,1,0), area 6935.5mm2, adj f22,f23,f26,f27,f38,f39,f40,f41
  f2: plane 203.2x38.1mm, normal (-1,0,0), area 6935.5mm2, adj f22,f23,f24,f27,f33,f34,f35,f36
  f3: plane 203.2x38.1mm, normal (0,-1,0), area 6935.5mm2, adj f22,f23,f24,f25,f28,f29,f30,f31
  f4: plane 260.35x260.35mm, normal (0,0,-1), area 3119mm2, adj f5,f6,f7,f8,f9,f10,f11,f12
  f5: plane 203.2x25.4mm, normal (0,1,0), area 5161.3mm2, adj f4,f6,f12,f13
  f6: cylinder r=25.4mm len=25.4mm, axis (0,0,-1), area 1013.4mm2, adj f4,f5,f7,f13
  f7: plane 203.2x25.4mm, normal (1,0,0), area 5161.3mm2, adj f4,f6,f8,f13
  f8: cylinder r=25.4mm len=25.4mm, axis (0,0,-1), area 1013.4mm2, adj f4,f7,f9,f13
  f9: plane 203.2x25.4mm, normal (0,-1,0), area 5161.3mm2, adj f4,f8,f10,f13
  f10: cylinder r=25.4mm len=25.4mm, axis (0,0,-1), area 1013.4mm2, adj f4,f9,f11,f13
  f11: plane 203.2x25.4mm, normal (-1,0,0), area 5161.3mm2, adj f4,f10,f12,f13
  f12: cylinder r=25.4mm len=25.4mm, axis (0,0,-1), area 1013.4mm2, adj f4,f5,f11,f13
  f13: plane 254x254mm, normal (0,0,-1), area 63962.2mm2, adj f5,f6,f7,f8,f9,f10,f11,f12
  f14: cylinder r=28.57mm len=28.58mm, axis (0,0,1), area 285mm2, adj f4,f15,f21,f22
  f15: plane 203.2x6.35mm, normal (0,1,0), area 1290.3mm2, adj f4,f14,f16,f22
  f16: cylinder r=28.57mm len=28.58mm, axis (0,0,1), area 285mm2, adj f4,f15,f17,f22
  f17: plane 203.2x6.35mm, normal (-1,0,0), area 1290.3mm2, adj f4,f16,f18,f22
  f18: cylinder r=28.57mm len=28.58mm, axis (0,0,1), area 285mm2, adj f4,f17,f19,f22
  f19: plane 203.2x6.35mm, normal (0,-1,0), area 1290.3mm2, adj f4,f18,f20,f22
  f20: cylinder r=28.57mm len=28.58mm, axis (0,0,1), area 285mm2, adj f4,f19,f21,f22
  f21: plane 203.2x6.35mm, normal (1,0,0), area 1290.3mm2, adj f4,f14,f20,f22
  f22: plane 266.7x266.7mm, normal (0,0,-1), area 3182.4mm2, adj f0,f1,f2,f3,f14,f15,f16,f17
  f23: plane 266.7x266.7mm, normal (0,0,1), area 70263.6mm2, adj f0,f1,f2,f3,f24,f25,f26,f27
  f24: cylinder r=31.75mm len=38.1mm, axis (0,0,-1), area 1900.2mm2, adj f2,f3,f22,f23
  f25: cylinder r=31.75mm len=38.1mm, axis (0,0,-1), area 1900.2mm2, adj f0,f3,f22,f23
  f26: cylinder r=31.75mm len=38.1mm, axis (0,0,-1), area 1900.2mm2, adj f0,f1,f22,f23
  f27: cylinder r=31.75mm len=38.1mm, axis (0,0,-1), area 1900.2mm2, adj f1,f2,f22,f23
  f28: plane 12.7x3.18mm, normal (-1,0,0), area 40.3mm2, adj f3,f29,f31,f32
  f29: plane 63.5x3.18mm, normal (0,0,-1), area 201.6mm2, adj f3,f28,f30,f32
  f30: plane 12.7x3.18mm, normal (1,0,0), area 40.3mm2, adj f3,f29,f31,f32
  f31: plane 63.5x3.18mm, normal (0,0,1), area 201.6mm2, adj f3,f28,f30,f32
  f32: plane 63.5x12.7mm, normal (0,-1,0), area 806.4mm2, adj f28,f29,f30,f31
  f33: plane 12.7x3.18mm, normal (0,1,0), area 40.3mm2, adj f2,f34,f36,f37
  f34: plane 63.5x3.18mm, normal (0,0,-1), area 201.6mm2, adj f2,f33,f35,f37
  f35: plane 12.7x3.18mm, normal (0,-1,0), area 40.3mm2, adj f2,f34,f36,f37
  f36: plane 63.5x3.18mm, normal (0,0,1), area 201.6mm2, adj f2,f33,f35,f37
  f37: plane 63.5x12.7mm, normal (-1,0,0), area 806.4mm2, adj f33,f34,f35,f36
  f38: plane 12.7x3.18mm, normal (1,0,0), area 40.3mm2, adj f1,f39,f41,f42
  f39: plane 63.5x3.18mm, normal (0,0,-1), area 201.6mm2, adj f1,f38,f40,f42
  f40: plane 12.7x3.18mm, normal (-1,0,0), area 40.3mm2, adj f1,f39,f41,f42
  f41: plane 63.5x3.18mm, normal (0,0,1), area 201.6mm2, adj f1,f38,f40,f42
  f42: plane 63.5x12.7mm, normal (0,1,0), area 806.4mm2, adj f38,f39,f40,f41
  f43: plane 12.7x3.18mm, normal (0,-1,0), area 40.3mm2, adj f0,f44,f46,f47
  f44: plane 63.5x3.18mm, normal (0,0,-1), area 201.6mm2, adj f0,f43,f45,f47
  f45: plane 12.7x3.18mm, normal (0,1,0), area 40.3mm2, adj f0,f44,f46,f47
  f46: plane 63.5x3.18mm, normal (0,0,1), area 201.6mm2, adj f0,f43,f45,f47
  f47: plane 63.5x12.7mm, normal (1,0,0), area 806.4mm2, adj f43,f44,f45,f46
PLACE A t=(-18.25,38.34,0.29)mm
PLACE B rot(axis=(1,0,0),180deg) t=(-18.25,38.34,139.99)mm
MATE fastened B.f13 <-> A.f275  axis (0,0,1) through (-18.25,38.34,-75.91)mm
